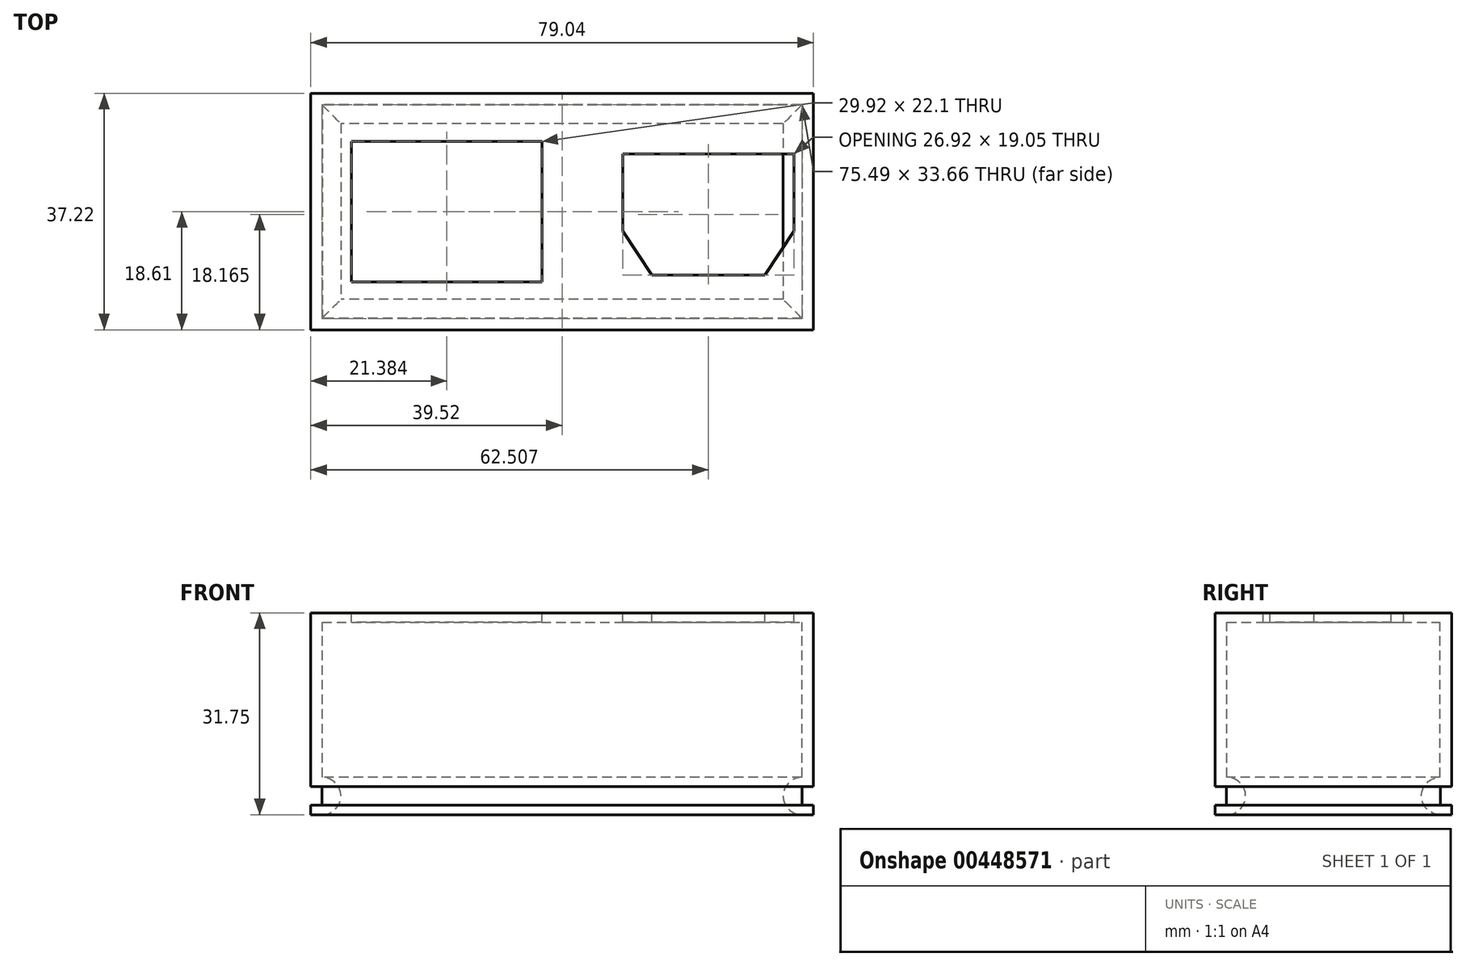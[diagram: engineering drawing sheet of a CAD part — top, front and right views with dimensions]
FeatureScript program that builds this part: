
annotation { "Feature Type Name" : "Feature", "Feature Type Description" : "" }
export const myFeature = defineFeature(function(context is Context, id is Id, definition is map)
    precondition{}
    {
        {
            var Q0;
            Q0=qCreatedBy(makeId("Top.planeOp"),FACE);
            var sketch = newSketch(context, id + "F0", { "sketchPlane" : qUnion([Q0])});
            skLineSegment(sketch, "E0.bottom", {"start": v(39.52, 18.6) * mm, "end": v(-39.52, 18.6) * mm});
            skLineSegment(sketch, "E0.top", {"start": v(39.52, -18.6) * mm, "end": v(-39.52, -18.6) * mm});
            skLineSegment(sketch, "E0.left", {"start": v(39.52, 18.6) * mm, "end": v(39.52, -18.6) * mm});
            skLineSegment(sketch, "E0.right", {"start": v(-39.52, 18.6) * mm, "end": v(-39.52, -18.6) * mm});
            skPoint(sketch, "E0.middle", {"position": v(0, 0) * mm});
            skLineSegment(sketch, "E1.bottom", {"start": v(-3.17, -11.05) * mm, "end": v(-33.1, -11.05) * mm});
            skLineSegment(sketch, "E1.top", {"start": v(-3.18, 11.05) * mm, "end": v(-33.1, 11.05) * mm});
            skLineSegment(sketch, "E1.left", {"start": v(-3.17, -11.05) * mm, "end": v(-3.18, 11.05) * mm});
            skLineSegment(sketch, "E1.right", {"start": v(-33.1, -11.05) * mm, "end": v(-33.1, 11.05) * mm});
            skPoint(sketch, "E1.middle", {"position": v(-18.14, 0) * mm});
            skLineSegment(sketch, "E2", {"start": v(36.45, 9.08) * mm, "end": v(9.52, 9.08) * mm});
            skLineSegment(sketch, "E3", {"start": v(9.52, 9.08) * mm, "end": v(9.53, -3.08) * mm});
            skLineSegment(sketch, "E4", {"start": v(9.53, -3.08) * mm, "end": v(14.1, -9.97) * mm});
            skLineSegment(sketch, "E5", {"start": v(14.1, -9.97) * mm, "end": v(31.88, -9.97) * mm});
            skLineSegment(sketch, "E6", {"start": v(36.45, 9.08) * mm, "end": v(36.45, -3.08) * mm});
            skLineSegment(sketch, "E7", {"start": v(36.45, -3.08) * mm, "end": v(31.88, -9.97) * mm});
            skLineSegment(sketch, "E8.bottom", {"start": v(-37.72, -16.76) * mm, "end": v(37.72, -16.76) * mm});
            skLineSegment(sketch, "E8.top", {"start": v(-37.72, 16.76) * mm, "end": v(37.72, 16.76) * mm});
            skLineSegment(sketch, "E8.left", {"start": v(-37.72, -16.76) * mm, "end": v(-37.72, 16.76) * mm});
            skLineSegment(sketch, "E8.right", {"start": v(37.72, -16.76) * mm, "end": v(37.72, 16.76) * mm});
            skSolve(sketch);
        }
        {
            var Q0;
            Q0=makeQuery(id+"F0.imprint","IMPRINT",FACE,{"disambiguationData":[TD([[makeQuery(id+"F0.imprint","IMPRINT",EDGE,{"derivedFrom":sQuery(id+"F0.wireOp",EDGE,"E0.bottom")}),1.0]])]});
            extrude(context, id + "F1", {"entities" : qUnion([Q0]), "oppositeDirection" : true, "depth" : 31.75 * mm, "offsetDistance" : 25.4 * mm});
        }
        {
            var Q0;
            Q0=makeQuery(id+"F0.imprint","IMPRINT",FACE,{"disambiguationData":[TD([[makeQuery(id+"F0.imprint","IMPRINT",EDGE,{"derivedFrom":sQuery(id+"F0.wireOp",EDGE,"E1.bottom")}),1.0]])]});
            extrude(context, id + "F2", {"entities" : qUnion([Q0]), "operationType" : NewBodyOperationType.ADD, "oppositeDirection" : true, "depth" : 1.47 * mm, "offsetDistance" : 25.4 * mm});
        }
        {
            var Q0;
            Q0=makeQuery(id+"F1.opExtrude","CAP_FACE",FACE,{"disambiguationData":[OSD([sQuery(id+"F0.wireOp",EDGE,"E0.bottom"),sQuery(id+"F0.wireOp",EDGE,"E0.top"),sQuery(id+"F0.wireOp",EDGE,"E0.left"),sQuery(id+"F0.wireOp",EDGE,"E0.right"),sQuery(id+"F0.wireOp",EDGE,"E8.bottom"),sQuery(id+"F0.wireOp",EDGE,"E8.top"),sQuery(id+"F0.wireOp",EDGE,"E8.left"),sQuery(id+"F0.wireOp",EDGE,"E8.right")])],"isStart":false});
            cPlane(context, id + "F3", {"entities" : qUnion([Q0]), "cplaneType" : CPlaneType.OFFSET, "offset" : 2.95 * mm, "oppositeDirection" : true, "width" : 152.4 * mm, "height" : 152.4 * mm});
        }
        {
            var Q0;
            Q0=makeQuery(id+"F1.opExtrude","SWEPT_FACE",FACE,{"disambiguationData":[OSD([sQuery(id+"F0.wireOp",EDGE,"E0.top")])]});
            var sketch = newSketch(context, id + "F4", { "sketchPlane" : qUnion([Q0])});
            skArc(sketch, "E9", {"start": v(-37.72, -31.75) * mm, "mid": v(-34.77, -28.8) * mm, "end": v(-37.72, -25.86) * mm});
            skLineSegment(sketch, "E10", {"start": v(-37.72, -25.86) * mm, "end": v(-37.72, -31.75) * mm});
            skLineSegment(sketch, "E11.MirrorCS", {"start": v(37.72, -25.86) * mm, "end": v(37.72, -31.75) * mm});
            skArc(sketch, "E12.MirrorCS", {"start": v(37.72, -31.75) * mm, "mid": v(34.77, -28.8) * mm, "end": v(37.72, -25.86) * mm});
            skSolve(sketch);
        }
        {
            var Q0;
            Q0 = qSketchRegion(id + "F4", true);
            var Q1;
            Q1=makeQuery(id+"F1.opExtrude","SWEPT_FACE",FACE,{"disambiguationData":[OSD([sQuery(id+"F0.wireOp",EDGE,"E8.top")])]});
            extrude(context, id + "F5", {"entities" : qUnion([Q0]), "operationType" : NewBodyOperationType.ADD, "endBound" : BoundingType.UP_TO_SURFACE, "oppositeDirection" : true, "depth" : 27.94 * mm, "endBoundEntityFace" : qUnion([Q1]), "offsetDistance" : 25.4 * mm});
        }
        {
            var Q0;
            Q0=makeQuery(id+"F1.opExtrude","SWEPT_FACE",FACE,{"disambiguationData":[OSD([sQuery(id+"F0.wireOp",EDGE,"E0.right")])]});
            var sketch = newSketch(context, id + "F6", { "sketchPlane" : qUnion([Q0])});
            skArc(sketch, "E13", {"start": v(-16.76, -31.75) * mm, "mid": v(-13.82, -28.8) * mm, "end": v(-16.76, -25.86) * mm});
            skLineSegment(sketch, "E14", {"start": v(-16.76, -25.86) * mm, "end": v(-16.76, -31.75) * mm});
            skLineSegment(sketch, "E15.MirrorCS", {"start": v(16.76, -25.86) * mm, "end": v(16.76, -31.75) * mm});
            skArc(sketch, "E16.MirrorCS", {"start": v(16.76, -31.75) * mm, "mid": v(13.82, -28.8) * mm, "end": v(16.76, -25.86) * mm});
            skSolve(sketch);
        }
        {
            var Q0;
            Q0 = qSketchRegion(id + "F6", true);
            var Q1;
            Q1=makeQuery(id+"F1.opExtrude","SWEPT_FACE",FACE,{"disambiguationData":[OSD([sQuery(id+"F0.wireOp",EDGE,"E8.right")])]});
            extrude(context, id + "F7", {"entities" : qUnion([Q0]), "operationType" : NewBodyOperationType.ADD, "endBound" : BoundingType.UP_TO_SURFACE, "oppositeDirection" : true, "depth" : 25.4 * mm, "endBoundEntityFace" : qUnion([Q1]), "offsetDistance" : 25.4 * mm});
        }
        {
            var Q0;
            Q0=makeQuery(id+"F1.opExtrude","SWEPT_FACE",FACE,{"disambiguationData":[OSD([sQuery(id+"F0.wireOp",EDGE,"E0.top")])]});
            var sketch = newSketch(context, id + "F8", { "sketchPlane" : qUnion([Q0])});
            skLineSegment(sketch, "E17.top", {"start": v(-39.52, -30.28) * mm, "end": v(-37.74, -30.28) * mm});
            skLineSegment(sketch, "E17.left", {"start": v(-39.52, -30.28) * mm, "end": v(-39.52, -27.33) * mm});
            skLineSegment(sketch, "E17.right", {"start": v(-37.74, -30.28) * mm, "end": v(-37.74, -27.33) * mm});
            skLineSegment(sketch, "E18", {"start": v(-39.52, -27.33) * mm, "end": v(-37.74, -27.33) * mm});
            skLineSegment(sketch, "E19.MirrorCS", {"start": v(39.52, -27.33) * mm, "end": v(37.74, -27.33) * mm});
            skLineSegment(sketch, "E20.MirrorCS", {"start": v(39.52, -30.28) * mm, "end": v(37.74, -30.28) * mm});
            skLineSegment(sketch, "E21.MirrorCS", {"start": v(39.52, -30.28) * mm, "end": v(39.52, -27.33) * mm});
            skLineSegment(sketch, "E22.MirrorCS", {"start": v(37.74, -30.28) * mm, "end": v(37.74, -27.33) * mm});
            skSolve(sketch);
        }
        {
            var Q0;
            Q0 = qSketchRegion(id + "F8", true);
            extrude(context, id + "F9", {"entities" : qUnion([Q0]), "operationType" : NewBodyOperationType.REMOVE, "endBound" : BoundingType.UP_TO_NEXT, "oppositeDirection" : true, "depth" : 25.4 * mm, "offsetDistance" : 25.4 * mm});
        }
        {
            var Q0;
            Q0=makeQuery(id+"F9.boolean.opBoolean","COPY",FACE,{"derivedFrom":makeQuery(id+"F9.opExtrude","SWEPT_FACE",FACE,{"disambiguationData":[OSD([sQuery(id+"F8.wireOp",EDGE,"E17.right")])]})});
            var sketch = newSketch(context, id + "F10", { "sketchPlane" : qUnion([Q0])});
            skLineSegment(sketch, "E23.bottom", {"start": v(-18.6, -30.28) * mm, "end": v(-16.83, -30.28) * mm});
            skLineSegment(sketch, "E23.top", {"start": v(-18.6, -27.33) * mm, "end": v(-16.83, -27.33) * mm});
            skLineSegment(sketch, "E23.left", {"start": v(-18.6, -30.28) * mm, "end": v(-18.6, -27.33) * mm});
            skLineSegment(sketch, "E23.right", {"start": v(-16.83, -30.28) * mm, "end": v(-16.83, -27.33) * mm});
            skLineSegment(sketch, "E24.MirrorCS", {"start": v(18.6, -30.28) * mm, "end": v(16.83, -30.28) * mm});
            skLineSegment(sketch, "E25.MirrorCS", {"start": v(16.83, -30.28) * mm, "end": v(16.83, -27.33) * mm});
            skLineSegment(sketch, "E26.MirrorCS", {"start": v(18.6, -27.33) * mm, "end": v(16.83, -27.33) * mm});
            skLineSegment(sketch, "E27.MirrorCS", {"start": v(18.6, -30.28) * mm, "end": v(18.6, -27.33) * mm});
            skSolve(sketch);
        }
        {
            var Q0;
            Q0 = qSketchRegion(id + "F10", true);
            extrude(context, id + "F11", {"entities" : qUnion([Q0]), "operationType" : NewBodyOperationType.REMOVE, "endBound" : BoundingType.UP_TO_NEXT, "oppositeDirection" : true, "depth" : 25.4 * mm, "offsetDistance" : 25.4 * mm});
        }
    });
